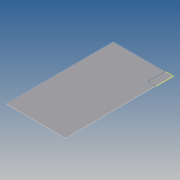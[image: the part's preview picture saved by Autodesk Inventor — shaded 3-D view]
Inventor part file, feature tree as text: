
AUTODESK INVENTOR PART (.ipt)
format: ipt  version: 2016 (Build 200138000, 138)  size: 70,144 bytes
history: native  units: mm
features: reference x4, plane x1, extrude x1, sketch x1
ambient origin geometry x8: Origin, YZ Plane, XZ Plane, XY Plane, X Axis, Y Axis, Z Axis, Center Point
bodies: Solid1 (feature_tree)
feature tree (7):
  plane  "Work Plane1"
  extrude  "Extrusion1"  [1 undecoded]
  sketch  "Sketch1"  dims[d0=0.5mm d1=0.0mm]
  reference  "Reference1"
  reference  "Reference2"
  reference  "Reference3"
  reference  "Reference4"
note: 1 required parameter value undecoded (feature->parameter linkage not recoverable at this tier; creation-order binding heuristic only, values carry confidence <= 0.55)
